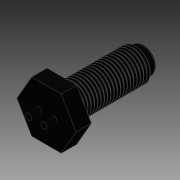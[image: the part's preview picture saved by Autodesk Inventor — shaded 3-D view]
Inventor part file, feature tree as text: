
AUTODESK INVENTOR PART (.ipt)
format: ipt  version: 2014 SP1 (Build 180222100, 222)  size: 523,776 bytes
history: native  units: in
note: dims shown in document units (in); Inventor stores cm internally (conversion verified against a paired STEP export)
features: extrude x5, sketch x4, fillet x1, helix x1, chamfer x1, projected_geometry x1
ambient origin geometry x8: Origin, YZ Plane, XZ Plane, XY Plane, X Axis, Y Axis, Z Axis, Center Point
bodies: Solid1 (feature_tree)
feature tree (13):
  sketch  "Sketch1"  dims[d0=1.25in d1=0.6875in]
  extrude  "Extrusion1"  Depth=0.6875in
  extrude  "Extrusion2"  Depth=1.8in TaperAngle=0.0deg
  sketch  "Sketch2"  dims[d2=0.375in d3=0.0in d4=1.8in d5=0.0in]
  extrude  "Extrusion3"  Depth=0.2in TaperAngle=0.0deg
  fillet  "Fillet1"  Radius=0.0394in
  extrude  "Extrusion4"  Depth=1.8in
  helix  "Coil1"  [1 undecoded]
  extrude  "Extrusion5"  Depth=1.8in TaperAngle=0.0deg
  chamfer  "Chamfer1"  Distance=0.01in
  sketch  "Sketch3"  dims[d6=0.625in d7=0.2in d8=0.0in d11=0.0394in]
  sketch  "Sketch4"  dims[d12=0.15in d13=0.15in d14=0.375in d15=0.25in d16=0.0in d18=0.01in d20=60.0deg d22=0.06in d24=0.08in d25=2.0in d26=8.6614in d27=0.0in d28=90.0deg d29=90.0deg d30=0.0in d31=0.0in d32=1.0in d33=1.0in d34=0.0in d35=1.8in d36=0.02in d37=0.125in d38=45.0deg]
  projected_geometry  "Projected Loop1"
note: 1 required parameter value undecoded (feature->parameter linkage not recoverable at this tier; creation-order binding heuristic only, values carry confidence <= 0.55)
